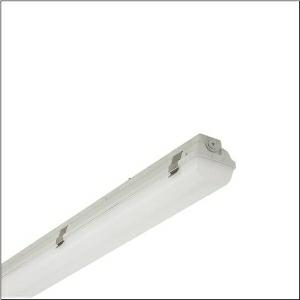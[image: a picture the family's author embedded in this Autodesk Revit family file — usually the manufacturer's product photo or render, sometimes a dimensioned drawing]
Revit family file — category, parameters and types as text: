
# Revit family: monsun_21_eco_51fj20ml45a
name_source: partatom
category: Lighting Fixtures
units: mm (PartAtom-declared; Revit-internal decimal feet)

## family parameters
Cut with Voids When Loaded = No
Host = Face
Light Source = No
Part Type = Normal
Room Calculation Point = No
Round Connector Dimension = Use Diameter
Shared = No

## types (1)
- --- (1 x LED, 4900 lm, 36 W, 4000K)
    Apparent Load = 36 VA
    CIE Flux Codes = 40 69 88 88 100
    Color Rendering = 80
    Color Temperature = 4000K
    Default Elevation = 1800 mm
    Description = Monsun 21 Eco, damp-proof luminaire, primary optical cover: diffuser, of PC, UV-stabilised, frosted, light emission: direct distribution, primary light characteristic: symmetric, installation type: suspended mounting, surface-mounted, LED, rated luminous flux: 4.900lm, luminous efficacy: 132lm/W, light colour: 840, colour temperature: 4000K, control gear: ON/OFF Multilumen, with terminal, 3-pole, max. 2.5mm², mains connection: 220..240V, AC, 50/60Hz, rated input power: 36W, housing, of glass-fibre reinforced polyester, light grey (RAL 7035), length: 1.277mm, width: 90mm, height: 95mm, clip for enclosure, of spring steel V2A, protection rating (complete): IP66, insulation class (complete): insulation class I (protective earthing), certification: CE, UKCA, protection symbol: D, impact resistance: IK08, permissible operating ambient temperature: -20..+35°C, corresponds to IFS (International Featured Standards) requirements for safety and quality in the food industry, contact your sales advisor before using the luminaires in applications with unclear chemical exposure, large temperature fluctuations or condensation-forming humidity, packaging unit: 1 piece
    Height = 103 mm
    Lamp = 1 x LED
    Lamp Light Flux = 4900 lm
    Lamp Power = 36 W
    Lamp count = 1
    Length = 1277 mm
    Luminous efficacy = 136 lm/W
    Manufacturer = Siteco
    ModVariant = No
    Model = 51FJ20ML45A
    Mounting Place = Ceiling
    Mounting Type = Surface mounted
    Number of Poles = 1
    OnlyDefault = Yes
    Power Factor = 1
    Product Name = Monsun 21 Eco
    Product group = damp-proof luminaire
    ProductGroupID = 300
    Protection Class = Protection class I
    Protection Degree = IP 66
    RLX_Detail_Level = 1
    RLX_Emergency_Light_Flux = 0 lm
    RLX_Emergency_Type = 0
    RLX_Emergency_Type_DB = No
    RlxData = <blob elided: 33961 chars, md5=d05b60df>
    Socket = socket
    Standby Power = 0 W
    System Light Flux = 4900 lm
    System Power = 36 W
    Type Comments = factory setting: luminous flux: 100 % | (ON | ON) | 350 mA
    Type Image = l_1007218.jpg
    URL = http://relux.com
    VarID = @adj_145681
    Voltage = 0 V
    Weight = 0.00 kg
    Width = 90 mm

## geometry (parser evidence)
native form markers: Blend x4, Sweep x11
no freeform markers — native parametric forms only
